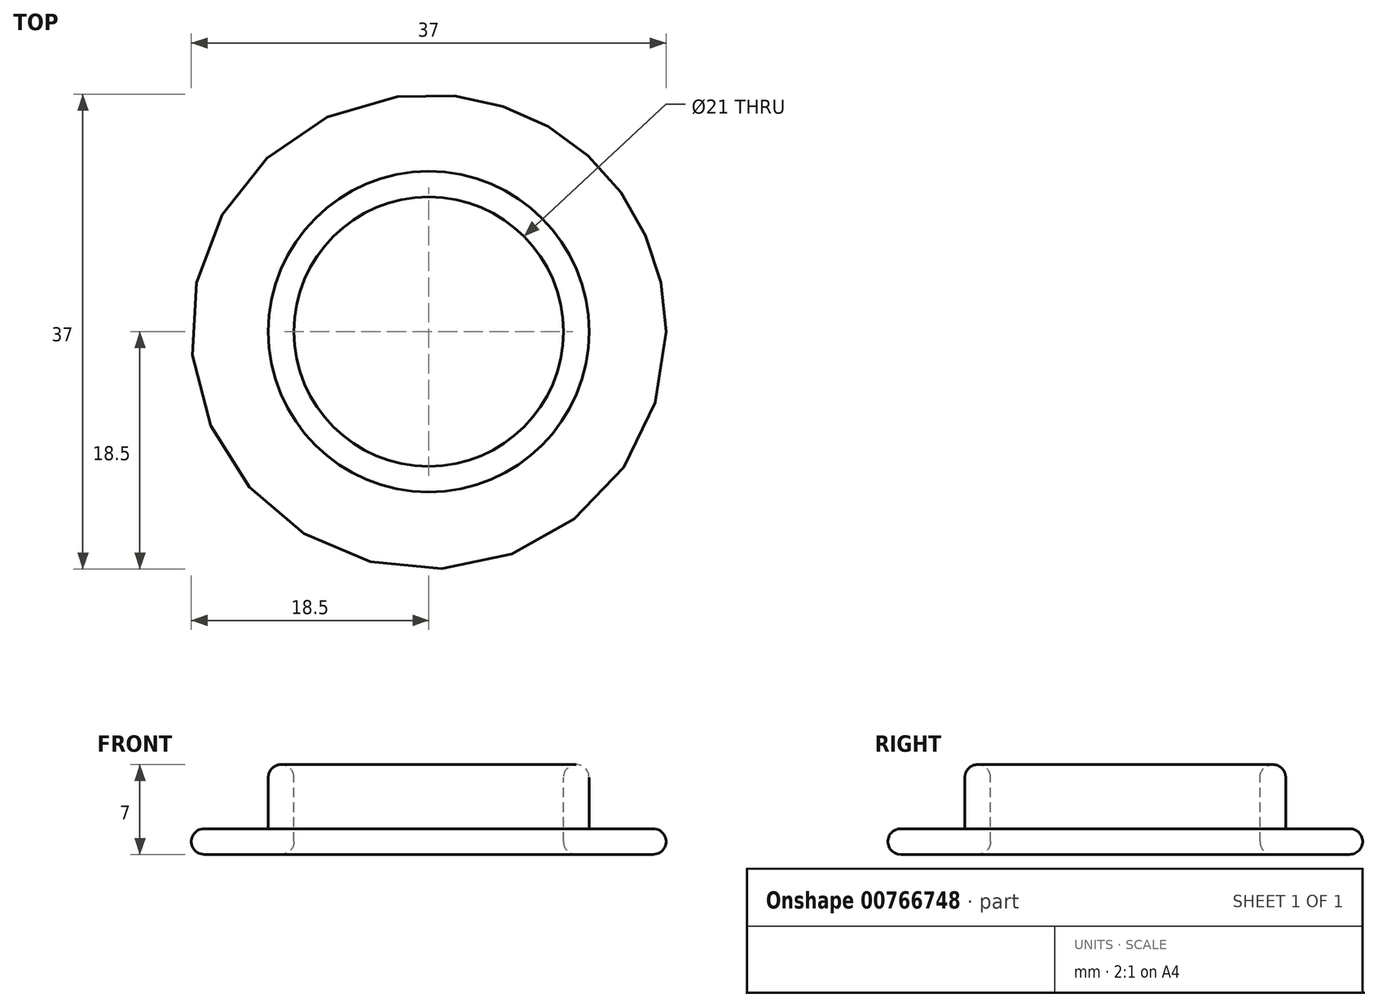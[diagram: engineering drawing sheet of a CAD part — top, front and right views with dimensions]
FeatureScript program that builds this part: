
annotation { "Feature Type Name" : "Feature", "Feature Type Description" : "" }
export const myFeature = defineFeature(function(context is Context, id is Id, definition is map)
    precondition{}
    {
        {
            var Q0;
            Q0=qCreatedBy(makeId("Top.planeOp"),FACE);
            var sketch = newSketch(context, id + "F0", { "sketchPlane" : qUnion([Q0])});
            skCircle(sketch, "E0", {"center": v(0, 0) * mm, "radius": 18.5 * mm});
            skSolve(sketch);
        }
        {
            var Q0;
            Q0=makeQuery(id+"F0.imprint","IMPRINT",FACE,{"disambiguationData":[TD([[makeQuery(id+"F0.imprint","IMPRINT",EDGE,{"derivedFrom":sQuery(id+"F0.wireOp",EDGE,"E0")}),1.0]])]});
            extrude(context, id + "F1", {"entities" : qUnion([Q0]), "depth" : 2 * mm, "offsetDistance" : 25 * mm});
        }
        {
            var Q0;
            Q0=makeQuery(id+"F1.opExtrude","CAP_FACE",FACE,{"disambiguationData":[OSD([sQuery(id+"F0.wireOp",EDGE,"E0")])],"isStart":false});
            var sketch = newSketch(context, id + "F2", { "sketchPlane" : qUnion([Q0])});
            skCircle(sketch, "E1", {"center": v(0, 0) * mm, "radius": 12.5 * mm});
            skSolve(sketch);
        }
        {
            var Q0;
            Q0=makeQuery(id+"F2.imprint","IMPRINT",FACE,{"disambiguationData":[TD([[makeQuery(id+"F2.imprint","IMPRINT",EDGE,{"derivedFrom":sQuery(id+"F2.wireOp",EDGE,"E1")}),1.0]])]});
            extrude(context, id + "F3", {"entities" : qUnion([Q0]), "operationType" : NewBodyOperationType.ADD, "depth" : 5 * mm, "offsetDistance" : 25 * mm});
        }
        {
            var Q0;
            Q0=makeQuery(id+"F3.opExtrude","CAP_FACE",FACE,{"disambiguationData":[OSD([sQuery(id+"F2.wireOp",EDGE,"E1")])],"isStart":false});
            var sketch = newSketch(context, id + "F4", { "sketchPlane" : qUnion([Q0])});
            skCircle(sketch, "E2", {"center": v(0, 0) * mm, "radius": 10.5 * mm});
            skSolve(sketch);
        }
        {
            var Q0;
            Q0=makeQuery(id+"F4.imprint","IMPRINT",FACE,{"disambiguationData":[TD([[makeQuery(id+"F4.imprint","IMPRINT",EDGE,{"derivedFrom":sQuery(id+"F4.wireOp",EDGE,"E2")}),1.0]])]});
            extrude(context, id + "F5", {"entities" : qUnion([Q0]), "operationType" : NewBodyOperationType.REMOVE, "oppositeDirection" : true, "depth" : 25 * mm, "offsetDistance" : 25 * mm});
        }
        {
            var Q0;
            Q0=makeQuery(id+"F1.opExtrude","CAP_FACE",FACE,{"disambiguationData":[OSD([sQuery(id+"F0.wireOp",EDGE,"E0")])],"isStart":true});
            fillet(context, id + "F6", {"entities" : qUnion([Q0]), "radius" : 1 * mm, "tangentPropagation" : true, "allowEdgeOverflow" : false});
        }
        {
            var Q0;
            Q0=makeQuery(id+"F3.opExtrude","CAP_FACE",FACE,{"disambiguationData":[OSD([sQuery(id+"F2.wireOp",EDGE,"E1")])],"isStart":false});
            fillet(context, id + "F7", {"entities" : qUnion([Q0]), "radius" : 1 * mm, "tangentPropagation" : true, "allowEdgeOverflow" : false});
        }
        {
            var Q0;
            Q0=makeQuery(id+"F1.opExtrude","CAP_EDGE",EDGE,{"disambiguationData":[OSD([sQuery(id+"F0.wireOp",EDGE,"E0")])],"isStart":false});
            fillet(context, id + "F8", {"entities" : qUnion([Q0]), "radius" : 1 * mm, "tangentPropagation" : true, "allowEdgeOverflow" : false});
        }
    });
